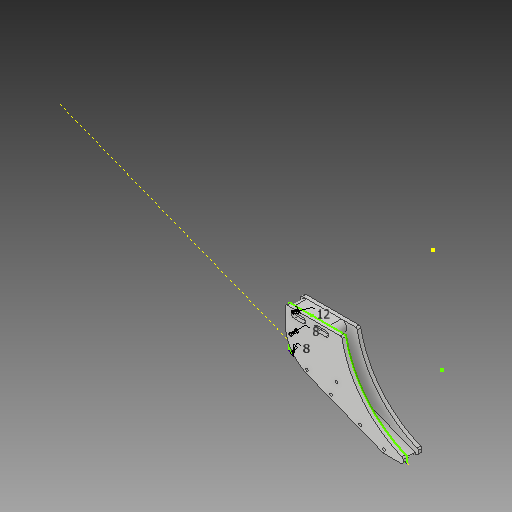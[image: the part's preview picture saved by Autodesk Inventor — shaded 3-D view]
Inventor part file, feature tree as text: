
AUTODESK INVENTOR PART (.ipt)
format: ipt  version: 2019.3 (Build 233278000, 278)  size: 258,048 bytes
history: native  units: mm
features: other x7, extrude x4, sketch x4, fillet x2, reference x2, projected_geometry x2
ambient origin geometry x8: Origin, YZ Plane, XZ Plane, XY Plane, X Axis, Y Axis, Z Axis, Center Point
bodies: Body1 (feature_tree), Body2 (feature_tree), Body3 (feature_tree)
feature tree (21):
  other  "ChainGuide-PlateBack"
  extrude  "Extrusion2"  Depth=12.0mm
  fillet  "Fillet4"  Radius=8.0mm
  extrude  "Extrusion8"  Depth=40.0mm
  extrude  "Extrusion9"  Depth=4.0mm TaperAngle=0.0deg
  fillet  "Fillet5"  Radius=2.0mm
  extrude  "Extrusion10"  Depth=10.0mm
  sketch  "Sketch1"  dims[d2=4.0mm d3=0.0mm d6=12.0mm d8=8.0mm]
  reference  "Reference1"
  sketch  "Sketch8"  dims[d9=8.0mm d33=40.0mm]
  projected_geometry  "Projected Loop2"
  reference  "Reference2"
  sketch  "Sketch9"  dims[d34=13.0mm d35=0.0mm d36=4.0mm d37=0.0mm d39=2.0mm]
  projected_geometry  "Projected Loop3"
  other  "ChainGuide-Middle"
  other  "ChainGuide-PlateFront"
  sketch  "Sketch11"  dims[d40=0.75mm d43=10.0mm d44=6.0mm d45=10.0mm d46=6.0mm d47=3.0mm d48=3.0mm d49=3.0mm d50=3.0mm d51=3.0mm d52=3.0mm d53=0.0mm d54=0.0mm]
  other  "<userpath>\Desktop\3dprojects\OpenEmoto\OpenEmoto.iam"
  other  "OpenEmoto.iam"
  other  "Swingarm3:1"
  other  "TestChain:1"
